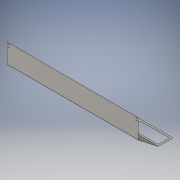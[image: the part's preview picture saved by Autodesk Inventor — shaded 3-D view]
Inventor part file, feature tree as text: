
AUTODESK INVENTOR PART (.ipt)
format: ipt  version: 2016 (Build 200138000, 138)  size: 194,048 bytes
history: native  units: mm
features: sheet_metal_op x7, sketch x5, other x5, hole x1
ambient origin geometry x8: Origin, YZ Plane, XZ Plane, XY Plane, X Axis, Y Axis, Z Axis, Center Point
bodies: Solid1 (feature_tree)
feature tree (18):
  sheet_metal_op  "Face1"
  sheet_metal_op  "Flange1"
  sheet_metal_op  "Flange2"
  hole  "Hole1"  [1 undecoded]
  sketch  "Sketch1"  dims[d0=190.0mm d1=1695.0mm]
  other  "Plate1"
  sketch  "Sketch2"  dims[d2=1.6mm]
  other  "Plate2"
  sheet_metal_op  "Bend1"
  sheet_metal_op  "Corner1"
  sketch  "Sketch3"  dims[d3=1.6mm]
  other  "Plate3"
  sheet_metal_op  "Bend2"
  sheet_metal_op  "Corner2"
  sketch  "Sketch4"  dims[d4=0.8mm]
  sketch  "Sketch5"  dims[d5=3.2mm d6=1.6mm d7=330.0mm d8=6.632251mm d9=1.6mm d10=6.4mm d11=1.6mm d12=1.6mm d13=1.6mm d14=0.8mm d15=3.2mm d16=1.6mm d17=250.0mm d18=9.075712mm d19=1.6mm d20=6.4mm d21=1.6mm d22=1.6mm d23=60.0mm d24=12.0mm d25=12.0mm d26=25.0mm d27=25.0mm d28=15.0mm d29=15.0mm d30=12.0mm d31=12.0mm d32=25.0mm d33=25.0mm d34=12.0mm d35=6.0mm d36=4.0mm d37=2.0mm d38=90.0deg d39=1.6mm d40=20.594885mm d41=15.0mm d42=15.0mm d43=422.0mm d44=23.0mm d45=23.0mm d46=23.0mm d47=23.0mm d48=1.6mm d49=0.0mm]
  other  "Cut1"
  other  "Definition1"
note: 1 required parameter value undecoded (feature->parameter linkage not recoverable at this tier; creation-order binding heuristic only, values carry confidence <= 0.55)
